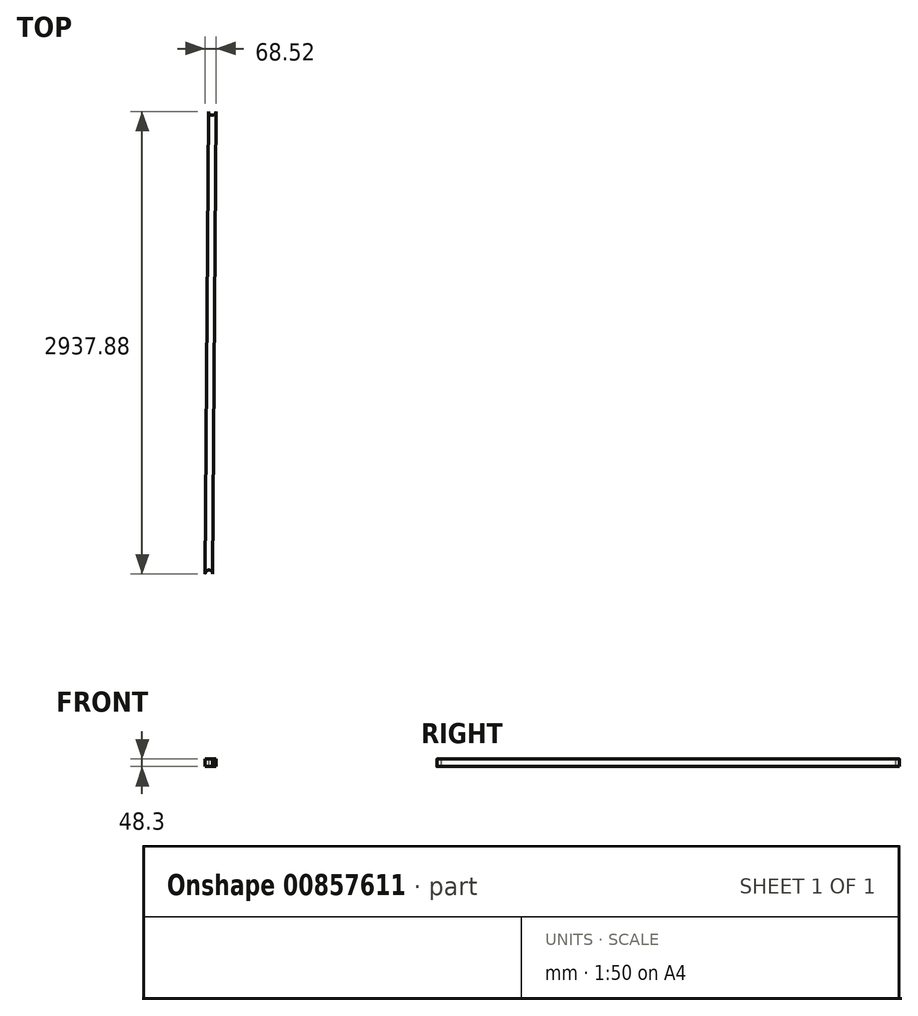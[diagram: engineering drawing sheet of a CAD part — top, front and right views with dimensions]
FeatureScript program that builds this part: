
annotation { "Feature Type Name" : "Feature", "Feature Type Description" : "" }
export const myFeature = defineFeature(function(context is Context, id is Id, definition is map)
    precondition{}
    {
        {
            var Q0;
            Q0=qCreatedBy(makeId("Top.planeOp"),FACE);
            var sketch = newSketch(context, id + "F0", { "sketchPlane" : qUnion([Q0])});
            skLineSegment(sketch, "E0.left", {"start": v(34.26, 1468.41) * mm, "end": v(14.03, -1468.94) * mm});
            skLineSegment(sketch, "E0.right", {"start": v(-14.03, 1468.94) * mm, "end": v(-34.26, -1468.41) * mm});
            skPoint(sketch, "E0.middle", {"position": v(0, 0) * mm});
            skArc(sketch, "E1", {"start": v(-14.03, 1468.94) * mm, "mid": v(9.85, 1444.62) * mm, "end": v(34.26, 1468.41) * mm});
            skArc(sketch, "E2", {"start": v(14.03, -1468.94) * mm, "mid": v(-9.85, -1444.43) * mm, "end": v(-34.26, -1468.41) * mm});
            skSolve(sketch);
        }
        {
            var Q0;
            Q0=qSketchRegion(id+"F0",true);
            extrude(context, id + "F1", {"entities" : qUnion([Q0]), "endBound" : BoundingType.SYMMETRIC, "depth" : 48.3 * mm, "offsetDistance" : 25 * mm});
        }
    });
